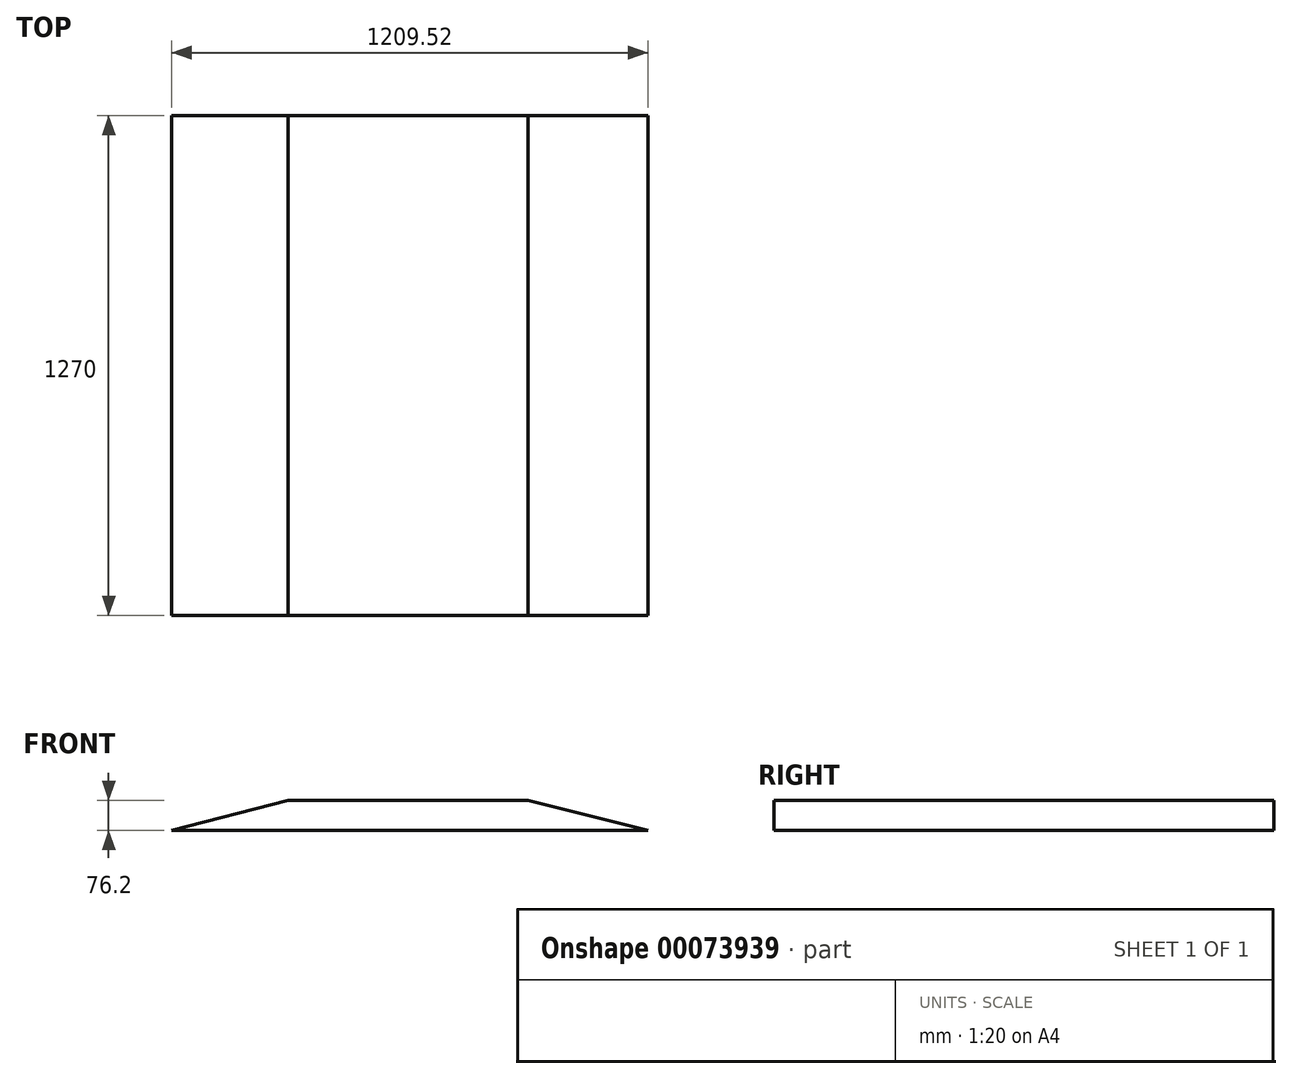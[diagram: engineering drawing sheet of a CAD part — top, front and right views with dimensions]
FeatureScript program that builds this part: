
annotation { "Feature Type Name" : "Feature", "Feature Type Description" : "" }
export const myFeature = defineFeature(function(context is Context, id is Id, definition is map)
    precondition{}
    {
        {
            var Q0;
            Q0=qCreatedBy(makeId("Front.planeOp"),FACE);
            var sketch = newSketch(context, id + "F0", { "sketchPlane" : qUnion([Q0])});
            skLineSegment(sketch, "E0.rect.bottom", {"start": v(-304.8, 38.1) * mm, "end": v(304.8, 38.1) * mm});
            skLineSegment(sketch, "E0.rect.top", {"start": v(-304.8, -38.1) * mm, "end": v(304.8, -38.1) * mm});
            skLineSegment(sketch, "E0.rect.left", {"start": v(-304.8, 38.1) * mm, "end": v(-304.8, -38.1) * mm});
            skLineSegment(sketch, "E0.rect.right", {"start": v(304.8, 38.1) * mm, "end": v(304.8, -38.1) * mm});
            skPoint(sketch, "E0.rect.middle", {"position": v(0, 0) * mm});
            skLineSegment(sketch, "E1", {"start": v(-304.8, 38.1) * mm, "end": v(-599.92, -38.1) * mm});
            skLineSegment(sketch, "E2", {"start": v(304.8, 38.1) * mm, "end": v(609.6, -38.1) * mm});
            skLineSegment(sketch, "E3", {"start": v(-599.92, -38.1) * mm, "end": v(-304.8, -38.1) * mm});
            skLineSegment(sketch, "E4", {"start": v(304.8, -38.1) * mm, "end": v(609.6, -38.1) * mm});
            skSolve(sketch);
        }
        {
            var Q0;
            Q0 = qSketchRegion(id + "F0", true);
            extrude(context, id + "F1", {"entities" : qUnion([Q0]), "depth" : 1270 * mm});
        }
    });
